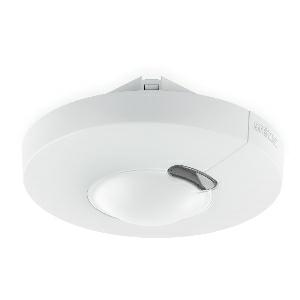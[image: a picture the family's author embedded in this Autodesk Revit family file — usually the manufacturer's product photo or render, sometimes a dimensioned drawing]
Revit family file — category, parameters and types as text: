
# Revit family: hf_3360_058241
name_source: partatom
category: Elektroinstallationen
revit_build: Autodesk Revit 2016 (Build: 20190508_0715(x64)
units: mm (PartAtom-declared; Revit-internal decimal feet)

## family parameters
Basisbauteil = Fläche
Beim Laden mit Abzugskörper schneiden = Nein
Bemaßung runder Anschluss = Durchmesser verwenden
Beschriftungsausrichtung beibehalten = Nein
Gemeinsam genutzt = Nein
Raumberechnungspunkt = Nein
Teiletyp = Normal

## types (1)
- HF 3360
    Apparent Load = 0 VA
    Beschreibung = Type: Motion detectors; Dimensions (Ø x H): 124 x 64 mm; Sensor Technology: High frequency; Application, place: Indoors; Application, room: function room / ancillary room, stairwell, WC / washroom, multi-storey / underground car park, Indoors; Installation site: wall, ceiling, corner; Installation: Concealed wiring; HF-system: 5,8 GHz; Mounting height: 2,00 – 4,00 m; Optimum mounting height: 2,8 m; Detection angle: 360 °; Sneak-by guard: Yes; Twilight setting TEACH: Yes; Time setting: 0 sec – 1092 min; Basic light level function: Yes; KNX functions: Photo-cell controller, Basic light level function, Light level, HVAC output, Constant-lighting control, Light output 2x, Presence output, Day / night function; With bus coupling: Yes; Settings via: ETS software, Remote control, Bus, Smart Remote; IP-rating: IP20; Material: Plastic; Colour: white; Colour, RAL: 9003; Version: KNX - concealed, rd.; PU1, EAN: 4007841058241
    Height = 0 mm  [stored 0 ft]
    Hersteller = Steinel
    Length = 124 mm  [stored 0.406824 ft]
    ModVariant = Nein
    Modell = 058241
    Mounting Type = Recessed
    Number of Poles = 1
    OnlyDefault = Ja
    Power Factor = 1
    Product Name = HF 3360
    Product group = Sensor-switched indoor light
    ProductGroupID = 30
    Protection Class = Protection class
    Protection Degree = IP 20
    RlxData = <blob elided: 35577 chars, md5=fa94107a>
    SensorDataFile = {"IESDataFiles":[]}
    Typenbild = produkt1_058241.jpg
    Typenkommentare = Product without accessories
    URL = http://relux.com
    VarID = ---
    Voltage = 0 V
    Vorgabe-Ansicht = 1800 mm
    Weight = 0.00 kg
    Width = 0 mm  [stored 0 ft]

note: [stored X ft] marks values corroborated as IEEE doubles in the binary element streams (Revit-internal decimal feet)

## geometry (parser evidence)
native form markers: Sweep x9
no freeform markers — native parametric forms only
